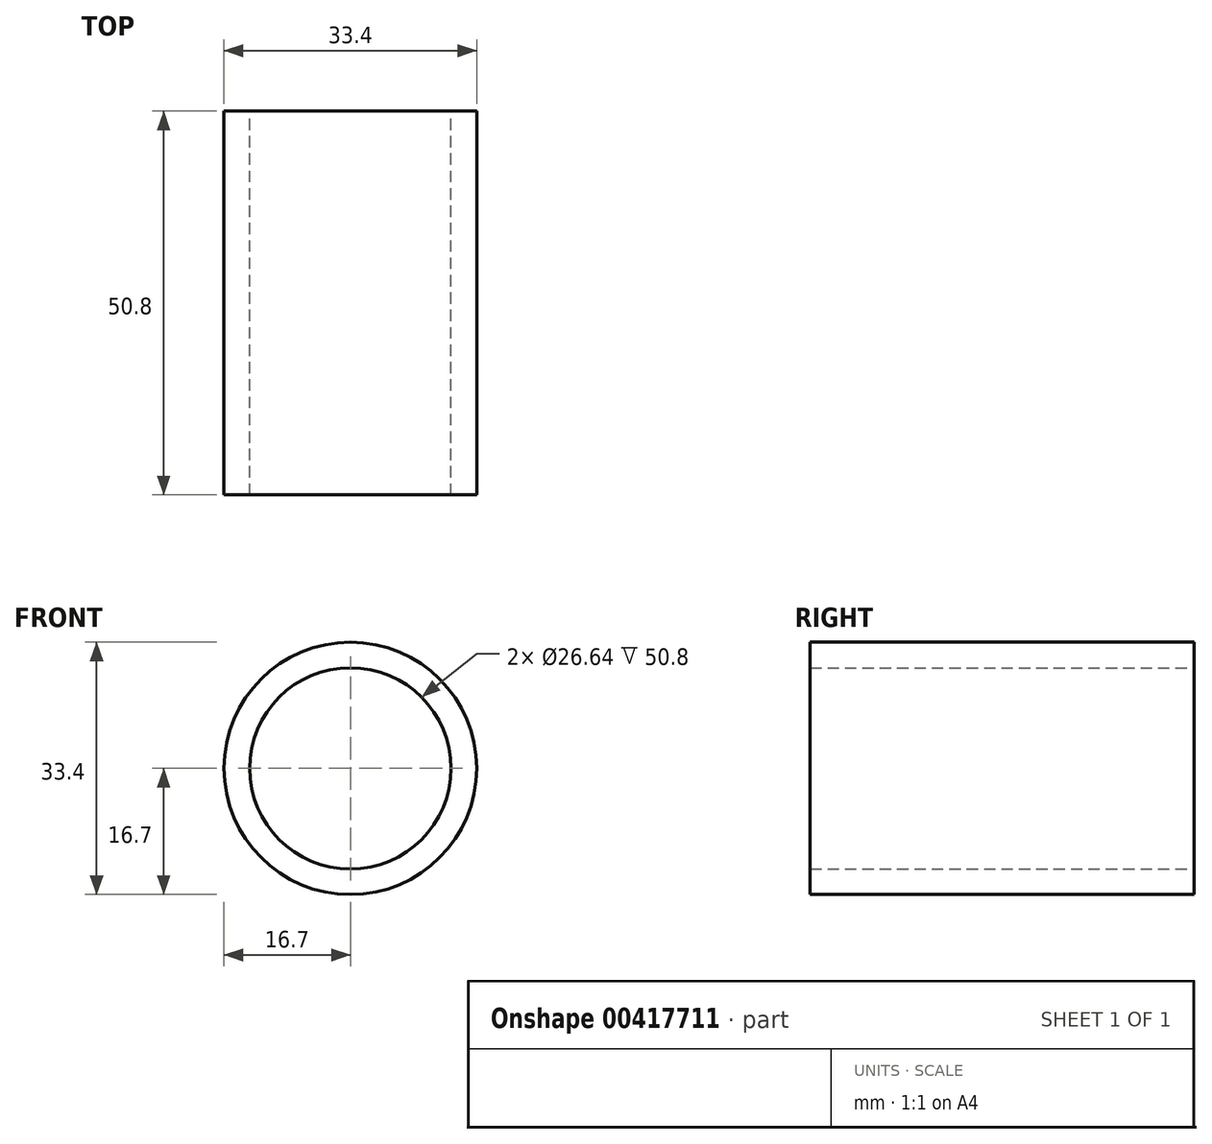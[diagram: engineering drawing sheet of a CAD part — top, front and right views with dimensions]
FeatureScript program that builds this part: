
annotation { "Feature Type Name" : "Feature", "Feature Type Description" : "" }
export const myFeature = defineFeature(function(context is Context, id is Id, definition is map)
    precondition{}
    {
        {
            var Q0;
            Q0=qCreatedBy(makeId("Front.planeOp"),FACE);
            var sketch = newSketch(context, id + "F0", { "sketchPlane" : qUnion([Q0])});
            skCircle(sketch, "E0", {"center": v(0, 0) * mm, "radius": 16.7 * mm});
            skCircle(sketch, "E1", {"center": v(0, 0) * mm, "radius": 13.32 * mm});
            skSolve(sketch);
        }
        {
            var Q0;
            Q0=makeQuery(id+"F0.imprint","IMPRINT",FACE,{"disambiguationData":[TD([[makeQuery(id+"F0.imprint","IMPRINT",EDGE,{"derivedFrom":sQuery(id+"F0.wireOp",EDGE,"E0")}),1.0]])]});
            extrude(context, id + "F1", {"entities" : qUnion([Q0]), "endBound" : BoundingType.SYMMETRIC, "depth" : 50.8 * mm});
        }
    });
